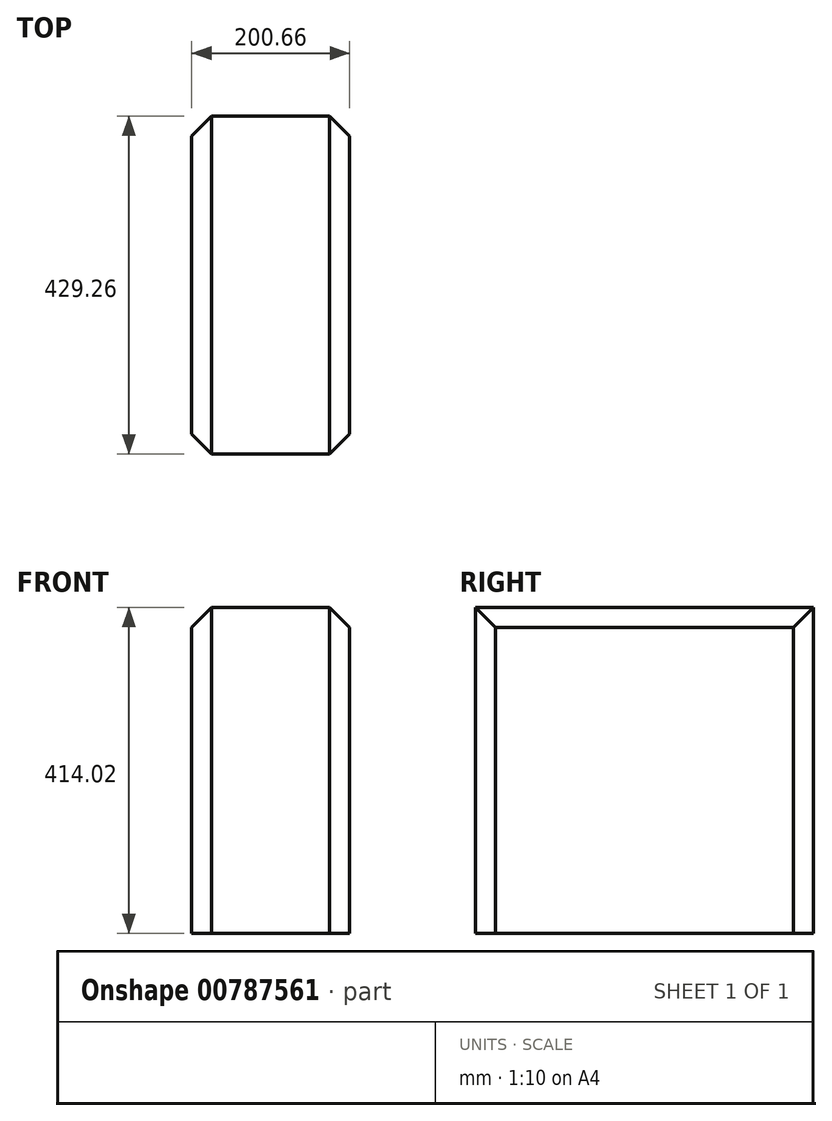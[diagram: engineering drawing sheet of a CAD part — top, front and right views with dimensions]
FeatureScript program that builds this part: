
annotation { "Feature Type Name" : "Feature", "Feature Type Description" : "" }
export const myFeature = defineFeature(function(context is Context, id is Id, definition is map)
    precondition{}
    {
        {
            var Q0;
            Q0=qCreatedBy(makeId("Top.planeOp"),FACE);
            var sketch = newSketch(context, id + "F0", { "sketchPlane" : qUnion([Q0])});
            skLineSegment(sketch, "E0.bottom", {"start": v(100.33, 214.63) * mm, "end": v(-100.33, 214.63) * mm});
            skLineSegment(sketch, "E0.top", {"start": v(100.33, -214.63) * mm, "end": v(-100.33, -214.63) * mm});
            skLineSegment(sketch, "E0.left", {"start": v(100.33, 214.63) * mm, "end": v(100.33, -214.63) * mm});
            skLineSegment(sketch, "E0.right", {"start": v(-100.33, 214.63) * mm, "end": v(-100.33, -214.63) * mm});
            skPoint(sketch, "E0.middle", {"position": v(0, 0) * mm});
            skSolve(sketch);
        }
        {
            var Q0;
            Q0=makeQuery(id+"F0.imprint","IMPRINT",FACE,{"disambiguationData":[TD([[makeQuery(id+"F0.imprint","IMPRINT",EDGE,{"derivedFrom":sQuery(id+"F0.wireOp",EDGE,"E0.bottom")}),1.0]])]});
            extrude(context, id + "F1", {"entities" : qUnion([Q0]), "depth" : 414.02 * mm, "offsetDistance" : 25.4 * mm});
        }
        {
            var Q0;
            Q0=makeQuery(id+"F1.opExtrude","CAP_EDGE",EDGE,{"disambiguationData":[OSD([sQuery(id+"F0.wireOp",EDGE,"E0.left")])],"isStart":false});
            var Q1;
            Q1=makeQuery(id+"F1.opExtrude","CAP_EDGE",EDGE,{"disambiguationData":[OSD([sQuery(id+"F0.wireOp",EDGE,"E0.right")])],"isStart":false});
            var Q2;
            Q2=makeQuery(id+"F1.opExtrude","SWEPT_EDGE",EDGE,{"disambiguationData":[OSD([sQuery(id+"F0.wireOp",EDGE,"E0.top"),sQuery(id+"F0.wireOp",EDGE,"E0.left")])]});
            var Q3;
            Q3=makeQuery(id+"F1.opExtrude","SWEPT_EDGE",EDGE,{"disambiguationData":[OSD([sQuery(id+"F0.wireOp",EDGE,"E0.bottom"),sQuery(id+"F0.wireOp",EDGE,"E0.left")])]});
            var Q4;
            Q4=makeQuery(id+"F1.opExtrude","SWEPT_EDGE",EDGE,{"disambiguationData":[OSD([sQuery(id+"F0.wireOp",EDGE,"E0.top"),sQuery(id+"F0.wireOp",EDGE,"E0.right")])]});
            var Q5;
            Q5=makeQuery(id+"F1.opExtrude","SWEPT_EDGE",EDGE,{"disambiguationData":[OSD([sQuery(id+"F0.wireOp",EDGE,"E0.bottom"),sQuery(id+"F0.wireOp",EDGE,"E0.right")])]});
            chamfer(context, id + "F2", {"entities" : qUnion([Q0, Q1, Q2, Q3, Q4, Q5]), "width" : 25.4 * mm, "tangentPropagation" : true});
        }
    });
